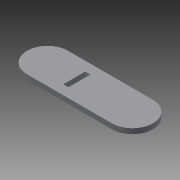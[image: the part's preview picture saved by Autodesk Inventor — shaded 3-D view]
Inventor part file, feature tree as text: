
AUTODESK INVENTOR PART (.ipt)
format: ipt  version: 2013 (Build 170138000, 138)  size: 99,840 bytes
history: native  units: mm
features: other x2, extrude x1, sketch x1
ambient origin geometry x8: Origin, YZ Plane, XZ Plane, XY Plane, X Axis, Y Axis, Z Axis, Center Point
feature tree (4):
  other  "Blocks"
  extrude  "Extrusion6"  Depth=3.0mm
  sketch  "Sketch1"  dims[d0=3.0mm d2=3.0mm d3=0.1mm d7=22.5mm d8=12.4mm d9=4.5mm d10=4.5mm d11=2.0mm d12=2.0mm d23=80.0mm d24=26.0mm d29=3.25mm d30=14.0mm d31=30.0mm d38=13.0mm d39=13.0mm d42=3.25mm d43=0.0mm]
  other  "Block1"
